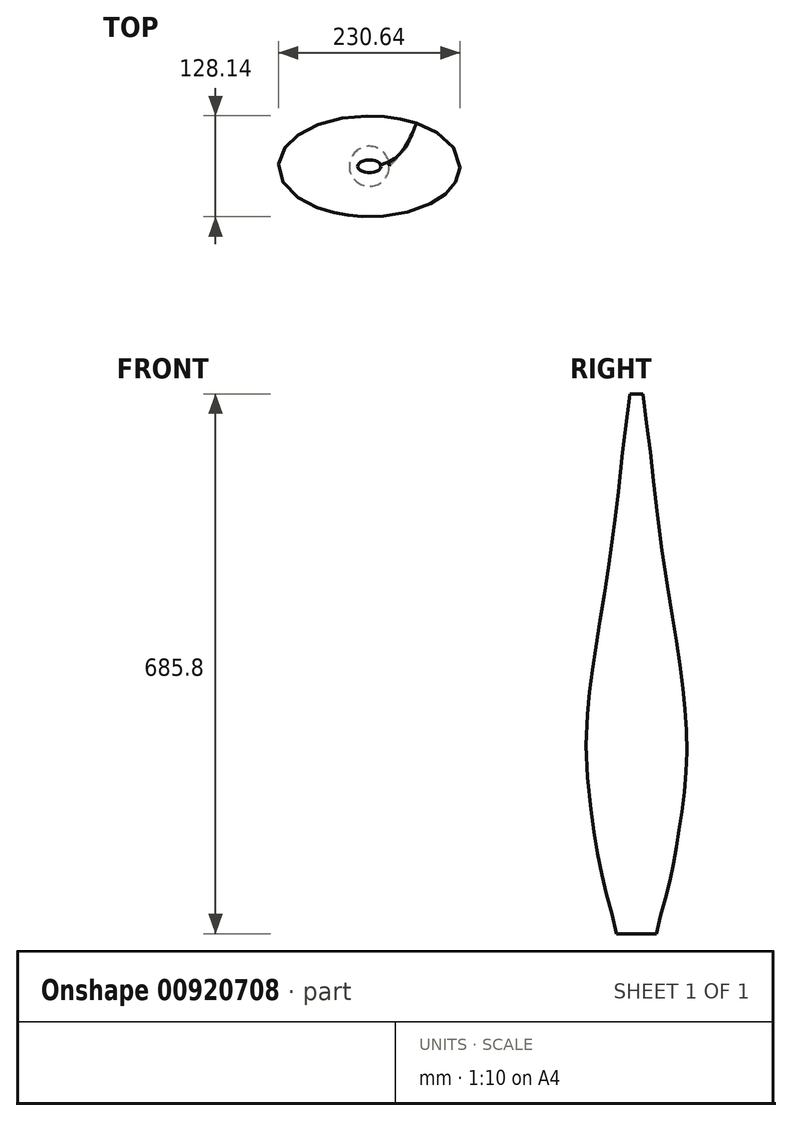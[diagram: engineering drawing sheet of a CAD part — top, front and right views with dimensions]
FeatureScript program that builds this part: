
annotation { "Feature Type Name" : "Feature", "Feature Type Description" : "" }
export const myFeature = defineFeature(function(context is Context, id is Id, definition is map)
    precondition{}
    {
        {
            var Q0;
            Q0=qCreatedBy(makeId("Top.planeOp"),FACE);
            var sketch = newSketch(context, id + "F0", { "sketchPlane" : qUnion([Q0])});
            skEllipse(sketch, "E0", {"center": v(0, 0) * mm, "majorRadius": 25.4 * mm, "minorRadius": 25.4 * mm, "majorAxis": v(1, 0)});
            skSolve(sketch);
        }
        {
            var Q0;
            Q0=qCreatedBy(makeId("Front.planeOp"),FACE);
            var sketch = newSketch(context, id + "F1", { "sketchPlane" : qUnion([Q0])});
            skLineSegment(sketch, "E1", {"start": v(0, 0) * mm, "end": v(0, 76.2) * mm, "construction": true});
            skPoint(sketch, "E2", {"position": v(0, 76.2) * mm});
            skPoint(sketch, "E3.0.1.0", {"position": v(0, 152.4) * mm});
            skPoint(sketch, "E3.0.2.0", {"position": v(0, 228.6) * mm});
            skPoint(sketch, "E3.0.3.0", {"position": v(0, 304.8) * mm});
            skPoint(sketch, "E3.0.4.0", {"position": v(0, 381) * mm});
            skPoint(sketch, "E3.0.5.0", {"position": v(0, 457.2) * mm});
            skPoint(sketch, "E3.0.6.0", {"position": v(0, 533.4) * mm});
            skPoint(sketch, "E3.0.7.0", {"position": v(0, 609.6) * mm});
            skPoint(sketch, "E3.0.8.0", {"position": v(0, 685.8) * mm});
            skLineSegment(sketch, "E3.direction1", {"start": v(0, 76.2) * mm, "end": v(25.4, 76.2) * mm, "construction": true});
            skLineSegment(sketch, "E3.direction2", {"start": v(0, 76.2) * mm, "end": v(0, 152.4) * mm, "construction": true});
            skSolve(sketch);
        }
        {
            var Q0;
            Q0=qCreatedBy(makeId("Top.planeOp"),FACE);
            var Q1;
            Q1=sQuery(id+"F1.wireOp",VERTEX,"E2");
            cPlane(context, id + "F2", {"entities" : qUnion([Q0, Q1]), "cplaneType" : CPlaneType.PLANE_POINT, "offset" : 25.4 * mm, "width" : 152.4 * mm, "height" : 152.4 * mm});
        }
        {
            var Q0;
            Q0=qCreatedBy(makeId("Top.planeOp"),FACE);
            var Q1;
            Q1=sQuery(id+"F1.wireOp",VERTEX,"E3.0.1.0");
            cPlane(context, id + "F3", {"entities" : qUnion([Q0, Q1]), "cplaneType" : CPlaneType.PLANE_POINT, "offset" : 25.4 * mm, "width" : 152.4 * mm, "height" : 152.4 * mm});
        }
        {
            var Q0;
            Q0=qCreatedBy(makeId("Top.planeOp"),FACE);
            var Q1;
            Q1=sQuery(id+"F1.wireOp",VERTEX,"E3.0.2.0");
            cPlane(context, id + "F4", {"entities" : qUnion([Q0, Q1]), "cplaneType" : CPlaneType.PLANE_POINT, "offset" : 25.4 * mm, "width" : 152.4 * mm, "height" : 152.4 * mm});
        }
        {
            var Q0;
            Q0=qCreatedBy(makeId("Top.planeOp"),FACE);
            var Q1;
            Q1=sQuery(id+"F1.wireOp",VERTEX,"E3.0.3.0");
            cPlane(context, id + "F5", {"entities" : qUnion([Q0, Q1]), "cplaneType" : CPlaneType.PLANE_POINT, "offset" : 25.4 * mm, "width" : 152.4 * mm, "height" : 152.4 * mm});
        }
        {
            var Q0;
            Q0=qCreatedBy(makeId("Top.planeOp"),FACE);
            var Q1;
            Q1=sQuery(id+"F1.wireOp",VERTEX,"E3.0.4.0");
            cPlane(context, id + "F6", {"entities" : qUnion([Q0, Q1]), "cplaneType" : CPlaneType.PLANE_POINT, "offset" : 25.4 * mm, "width" : 152.4 * mm, "height" : 152.4 * mm});
        }
        {
            var Q0;
            Q0=qCreatedBy(makeId("Top.planeOp"),FACE);
            var Q1;
            Q1=sQuery(id+"F1.wireOp",VERTEX,"E3.0.5.0");
            cPlane(context, id + "F7", {"entities" : qUnion([Q0, Q1]), "cplaneType" : CPlaneType.PLANE_POINT, "offset" : 25.4 * mm, "width" : 152.4 * mm, "height" : 152.4 * mm});
        }
        {
            var Q0;
            Q0=qCreatedBy(makeId("Top.planeOp"),FACE);
            var Q1;
            Q1=sQuery(id+"F1.wireOp",VERTEX,"E3.0.6.0");
            cPlane(context, id + "F8", {"entities" : qUnion([Q0, Q1]), "cplaneType" : CPlaneType.PLANE_POINT, "offset" : 25.4 * mm, "width" : 152.4 * mm, "height" : 152.4 * mm});
        }
        {
            var Q0;
            Q0=qCreatedBy(makeId("Top.planeOp"),FACE);
            var Q1;
            Q1=sQuery(id+"F1.wireOp",VERTEX,"E3.0.7.0");
            cPlane(context, id + "F9", {"entities" : qUnion([Q0, Q1]), "cplaneType" : CPlaneType.PLANE_POINT, "offset" : 25.4 * mm, "width" : 152.4 * mm, "height" : 152.4 * mm});
        }
        {
            var Q0;
            Q0=qCreatedBy(makeId("Top.planeOp"),FACE);
            var Q1;
            Q1=sQuery(id+"F1.wireOp",VERTEX,"E3.0.8.0");
            cPlane(context, id + "F10", {"entities" : qUnion([Q0, Q1]), "cplaneType" : CPlaneType.PLANE_POINT, "offset" : 25.4 * mm, "width" : 152.4 * mm, "height" : 152.4 * mm});
        }
        {
            var Q0;
            Q0=qCreatedBy(id+"F2.planeOp",FACE);
            var sketch = newSketch(context, id + "F11", { "sketchPlane" : qUnion([Q0])});
            skEllipse(sketch, "E4", {"center": v(0, 0) * mm, "majorRadius": 63.5 * mm, "minorRadius": 44.45 * mm, "majorAxis": v(1, 0)});
            skSolve(sketch);
        }
        {
            var Q0;
            Q0=qCreatedBy(id+"F3.planeOp",FACE);
            var sketch = newSketch(context, id + "F12", { "sketchPlane" : qUnion([Q0])});
            skEllipse(sketch, "E5", {"center": v(0, 0) * mm, "majorRadius": 102.74 * mm, "minorRadius": 57.15 * mm, "majorAxis": v(1, 0)});
            skSolve(sketch);
        }
        {
            var Q0;
            Q0=qCreatedBy(id+"F4.planeOp",FACE);
            var sketch = newSketch(context, id + "F13", { "sketchPlane" : qUnion([Q0])});
            skEllipse(sketch, "E6", {"center": v(0, 0) * mm, "majorRadius": 115.32 * mm, "minorRadius": 64 * mm, "majorAxis": v(1, 0)});
            skSolve(sketch);
        }
        {
            var Q0;
            Q0=qCreatedBy(id+"F5.planeOp",FACE);
            var sketch = newSketch(context, id + "F14", { "sketchPlane" : qUnion([Q0])});
            skEllipse(sketch, "E7", {"center": v(0, 0) * mm, "majorRadius": 107.44 * mm, "minorRadius": 59.7 * mm, "majorAxis": v(1, 0)});
            skSolve(sketch);
        }
        {
            var Q0;
            Q0=qCreatedBy(id+"F6.planeOp",FACE);
            var sketch = newSketch(context, id + "F15", { "sketchPlane" : qUnion([Q0])});
            skEllipse(sketch, "E8", {"center": v(0, 0) * mm, "majorRadius": 88.52 * mm, "minorRadius": 49.15 * mm, "majorAxis": v(1, 0)});
            skSolve(sketch);
        }
        {
            var Q0;
            Q0=qCreatedBy(id+"F7.planeOp",FACE);
            var sketch = newSketch(context, id + "F16", { "sketchPlane" : qUnion([Q0])});
            skEllipse(sketch, "E9", {"center": v(0, 0) * mm, "majorRadius": 66.3 * mm, "minorRadius": 36.83 * mm, "majorAxis": v(1, 0)});
            skSolve(sketch);
        }
        {
            var Q0;
            Q0=qCreatedBy(id+"F8.planeOp",FACE);
            var sketch = newSketch(context, id + "F17", { "sketchPlane" : qUnion([Q0])});
            skEllipse(sketch, "E10", {"center": v(0, 0) * mm, "majorRadius": 47.5 * mm, "minorRadius": 26.42 * mm, "majorAxis": v(1, 0)});
            skSolve(sketch);
        }
        {
            var Q0;
            Q0=qCreatedBy(id+"F9.planeOp",FACE);
            var sketch = newSketch(context, id + "F18", { "sketchPlane" : qUnion([Q0])});
            skEllipse(sketch, "E11", {"center": v(0, 0) * mm, "majorRadius": 31.75 * mm, "minorRadius": 17.78 * mm, "majorAxis": v(1, 0)});
            skSolve(sketch);
        }
        {
            var Q0;
            Q0=qCreatedBy(id+"F10.planeOp",FACE);
            var sketch = newSketch(context, id + "F19", { "sketchPlane" : qUnion([Q0])});
            skEllipse(sketch, "E12", {"center": v(0, 0) * mm, "majorRadius": 14.73 * mm, "minorRadius": 8.13 * mm, "majorAxis": v(1, 0)});
            skSolve(sketch);
        }
        {
            var Q0;
            Q0=makeQuery(id+"F0.imprint","IMPRINT",FACE,{"disambiguationData":[TD([[makeQuery(id+"F0.imprint","IMPRINT",EDGE,{"derivedFrom":sQuery(id+"F0.wireOp",EDGE,"E0")}),1.0]])]});
            var Q1;
            Q1=makeQuery(id+"F11.imprint","IMPRINT",FACE,{"disambiguationData":[TD([[makeQuery(id+"F11.imprint","IMPRINT",EDGE,{"derivedFrom":sQuery(id+"F11.wireOp",EDGE,"E4")}),1.0]])]});
            var Q2;
            Q2=makeQuery(id+"F12.imprint","IMPRINT",FACE,{"disambiguationData":[TD([[makeQuery(id+"F12.imprint","IMPRINT",EDGE,{"derivedFrom":sQuery(id+"F12.wireOp",EDGE,"E5")}),1.0]])]});
            var Q3;
            Q3=makeQuery(id+"F13.imprint","IMPRINT",FACE,{"disambiguationData":[TD([[makeQuery(id+"F13.imprint","IMPRINT",EDGE,{"derivedFrom":sQuery(id+"F13.wireOp",EDGE,"E6")}),1.0]])]});
            var Q4;
            Q4=makeQuery(id+"F14.imprint","IMPRINT",FACE,{"disambiguationData":[TD([[makeQuery(id+"F14.imprint","IMPRINT",EDGE,{"derivedFrom":sQuery(id+"F14.wireOp",EDGE,"E7")}),1.0]])]});
            var Q5;
            Q5=makeQuery(id+"F15.imprint","IMPRINT",FACE,{"disambiguationData":[TD([[makeQuery(id+"F15.imprint","IMPRINT",EDGE,{"derivedFrom":sQuery(id+"F15.wireOp",EDGE,"E8")}),1.0]])]});
            var Q6;
            Q6=makeQuery(id+"F16.imprint","IMPRINT",FACE,{"disambiguationData":[TD([[makeQuery(id+"F16.imprint","IMPRINT",EDGE,{"derivedFrom":sQuery(id+"F16.wireOp",EDGE,"E9")}),1.0]])]});
            var Q7;
            Q7=makeQuery(id+"F17.imprint","IMPRINT",FACE,{"disambiguationData":[TD([[makeQuery(id+"F17.imprint","IMPRINT",EDGE,{"derivedFrom":sQuery(id+"F17.wireOp",EDGE,"E10")}),1.0]])]});
            var Q8;
            Q8=makeQuery(id+"F18.imprint","IMPRINT",FACE,{"disambiguationData":[TD([[makeQuery(id+"F18.imprint","IMPRINT",EDGE,{"derivedFrom":sQuery(id+"F18.wireOp",EDGE,"E11")}),1.0]])]});
            var Q9;
            Q9=makeQuery(id+"F19.imprint","IMPRINT",FACE,{"disambiguationData":[TD([[makeQuery(id+"F19.imprint","IMPRINT",EDGE,{"derivedFrom":sQuery(id+"F19.wireOp",EDGE,"E12")}),1.0]])]});
            loft(context, id + "F20", {"sheetProfilesArray" : [{ "sheetProfileEntities" : qUnion([Q0]) }, { "sheetProfileEntities" : qUnion([Q1]) }, { "sheetProfileEntities" : qUnion([Q2]) }, { "sheetProfileEntities" : qUnion([Q3]) }, { "sheetProfileEntities" : qUnion([Q4]) }, { "sheetProfileEntities" : qUnion([Q5]) }, { "sheetProfileEntities" : qUnion([Q6]) }, { "sheetProfileEntities" : qUnion([Q7]) }, { "sheetProfileEntities" : qUnion([Q8]) }, { "sheetProfileEntities" : qUnion([Q9]) }]});
        }
    });
